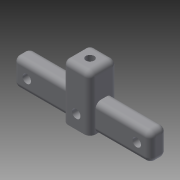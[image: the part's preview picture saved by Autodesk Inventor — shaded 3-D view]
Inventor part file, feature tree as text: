
AUTODESK INVENTOR PART (.ipt)
format: ipt  version: 2015 (Build 190159000, 159)  size: 192,000 bytes
history: native  units: mm
features: sketch x5, hole x3, fillet x3, extrude x2, plane x2, mirror x1
ambient origin geometry x8: Origin, YZ Plane, XZ Plane, XY Plane, X Axis, Y Axis, Z Axis, Center Point
bodies: Body1 (feature_tree)
feature tree (16):
  extrude  "Extrusion3"  Depth=10.0mm
  hole  "Hole4"  [1 undecoded]
  hole  "Hole5"  [1 undecoded]
  extrude  "Extrusion4"  Depth=6.0mm
  plane  "Work Plane2"
  hole  "Hole6"  [1 undecoded]
  plane  "Work Plane1"
  mirror  "Mirror1"
  fillet  "Fillet3"  Radius=5.0mm
  fillet  "Fillet4"  Radius=2.0mm
  fillet  "Fillet5"  Radius=2.0mm
  sketch  "Sketch6"  dims[d31=10.0mm d32=10.0mm]
  sketch  "Sketch7"  dims[d33=5.0mm d34=5.0mm]
  sketch  "Sketch8"  dims[d35=20.0mm d36=0.0mm]
  sketch  "Sketch9"  dims[d37=3.0mm d38=6.0mm d39=4.0mm d40=2.0mm d41=90.0deg d42=8.0mm d43=0.0mm d44=5.0mm]
  sketch  "Sketch10"  dims[d45=3.1mm d46=6.0mm d47=4.0mm d48=5.0mm d49=90.0deg d50=8.0mm d51=0.0mm d52=6.0mm d53=20.0mm d54=0.0mm d56=5.0mm d57=3.1mm d58=6.0mm d59=4.0mm d60=3.0mm d61=90.0deg d62=8.0mm d63=0.0mm d64=2.0mm d65=2.0mm d66=2.0mm]
note: 3 required parameter values undecoded (feature->parameter linkage not recoverable at this tier; creation-order binding heuristic only, values carry confidence <= 0.55)
